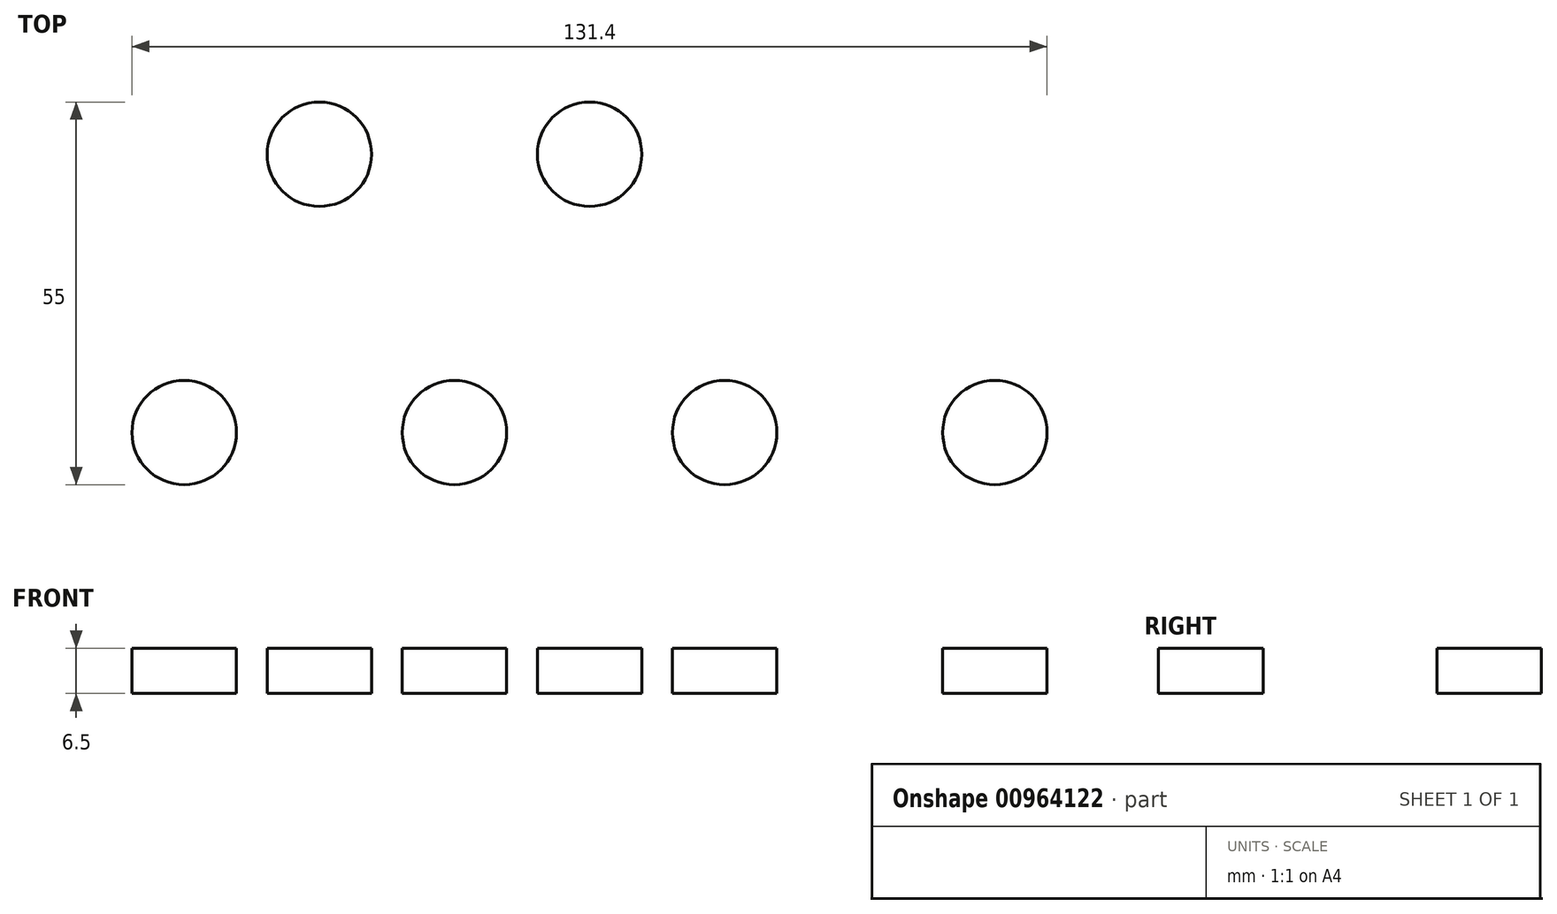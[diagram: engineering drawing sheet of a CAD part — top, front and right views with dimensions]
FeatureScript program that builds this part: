
annotation { "Feature Type Name" : "Feature", "Feature Type Description" : "" }
export const myFeature = defineFeature(function(context is Context, id is Id, definition is map)
    precondition{}
    {
        {
            var Q0;
            Q0=qCreatedBy(makeId("Top.planeOp"),FACE);
            var sketch = newSketch(context, id + "F0", { "sketchPlane" : qUnion([Q0])});
            skLineSegment(sketch, "E0.bottom", {"start": v(-80, 55) * mm, "end": v(80, 55) * mm});
            skLineSegment(sketch, "E0.top", {"start": v(-80, -55) * mm, "end": v(80, -55) * mm});
            skLineSegment(sketch, "E0.left", {"start": v(-80, 55) * mm, "end": v(-80, -55) * mm});
            skLineSegment(sketch, "E0.right", {"start": v(80, 55) * mm, "end": v(80, -55) * mm});
            skPoint(sketch, "E0.middle", {"position": v(0, 0) * mm});
            skSolve(sketch);
        }
        {
            var Q0;
            Q0=makeQuery(id+"F0.imprint","IMPRINT",FACE,{"disambiguationData":[TD([[makeQuery(id+"F0.imprint","IMPRINT",EDGE,{"derivedFrom":sQuery(id+"F0.wireOp",EDGE,"E0.bottom")}),-1.0]])]});
            extrude(context, id + "F1", {"entities" : qUnion([Q0]), "depth" : 6.5 * mm, "offsetDistance" : 25 * mm});
        }
        {
            var Q0;
            Q0=makeQuery(id+"F1.opExtrude","SWEPT_FACE",FACE,{"disambiguationData":[OSD([sQuery(id+"F0.wireOp",EDGE,"E0.left")])]});
            var sketch = newSketch(context, id + "F2", { "sketchPlane" : qUnion([Q0])});
            skLineSegment(sketch, "E1", {"start": v(-55, 3.25) * mm, "end": v(-35, 3.25) * mm});
            skLineSegment(sketch, "E2", {"start": v(-35, 3.25) * mm, "end": v(0, 3.25) * mm});
            skLineSegment(sketch, "E3", {"start": v(0, 3.25) * mm, "end": v(35, 3.25) * mm});
            skLineSegment(sketch, "E4", {"start": v(35, 3.25) * mm, "end": v(55, 3.25) * mm});
            skLineSegment(sketch, "E5.bottom", {"start": v(-39.75, 6.5) * mm, "end": v(-30.25, 6.5) * mm});
            skLineSegment(sketch, "E5.top", {"start": v(-39.75, 0) * mm, "end": v(-30.25, 0) * mm});
            skLineSegment(sketch, "E5.left", {"start": v(-39.75, 6.5) * mm, "end": v(-39.75, 0) * mm});
            skLineSegment(sketch, "E5.right", {"start": v(-30.25, 6.5) * mm, "end": v(-30.25, 0) * mm});
            skPoint(sketch, "E5.middle", {"position": v(-35, 3.25) * mm});
            skLineSegment(sketch, "E6.bottom", {"start": v(-4.75, 6.5) * mm, "end": v(4.75, 6.5) * mm});
            skLineSegment(sketch, "E6.top", {"start": v(-4.75, 0) * mm, "end": v(4.75, 0) * mm});
            skLineSegment(sketch, "E6.left", {"start": v(-4.75, 6.5) * mm, "end": v(-4.75, 0) * mm});
            skLineSegment(sketch, "E6.right", {"start": v(4.75, 6.5) * mm, "end": v(4.75, 0) * mm});
            skPoint(sketch, "E6.middle", {"position": v(0, 3.25) * mm});
            skLineSegment(sketch, "E7.bottom", {"start": v(39.75, 6.5) * mm, "end": v(30.25, 6.5) * mm});
            skLineSegment(sketch, "E7.top", {"start": v(39.75, 0) * mm, "end": v(30.25, 0) * mm});
            skLineSegment(sketch, "E7.left", {"start": v(39.75, 6.5) * mm, "end": v(39.75, 0) * mm});
            skLineSegment(sketch, "E7.right", {"start": v(30.25, 6.5) * mm, "end": v(30.25, 0) * mm});
            skPoint(sketch, "E7.middle", {"position": v(35, 3.25) * mm});
            skSolve(sketch);
        }
        {
            var Q0;
            {var subQ0=sQuery(id+"F2.wireOp",EDGE,"E5.bottom");Q0=makeQuery(id+"F2.imprint","IMPRINT",FACE,{"disambiguationData":[TD([[makeQuery(id+"F2.imprint","IMPRINT",EDGE,{"derivedFrom":subQ0}),-1.0]])]});}
            var Q1;
            {var subQ1=sQuery(id+"F2.wireOp",EDGE,"E5.top");Q1=makeQuery(id+"F2.imprint","IMPRINT",FACE,{"disambiguationData":[TD([[makeQuery(id+"F2.imprint","IMPRINT",EDGE,{"derivedFrom":subQ1}),1.0]])]});}
            var Q2;
            {var subQ1=sQuery(id+"F2.wireOp",EDGE,"E6.bottom");Q2=makeQuery(id+"F2.imprint","IMPRINT",FACE,{"disambiguationData":[TD([[makeQuery(id+"F2.imprint","IMPRINT",EDGE,{"derivedFrom":subQ1}),-1.0]])]});}
            var Q3;
            {var subQ0=sQuery(id+"F2.wireOp",EDGE,"E6.top");Q3=makeQuery(id+"F2.imprint","IMPRINT",FACE,{"disambiguationData":[TD([[makeQuery(id+"F2.imprint","IMPRINT",EDGE,{"derivedFrom":subQ0}),1.0]])]});}
            var Q4;
            {var subQ1=sQuery(id+"F2.wireOp",EDGE,"E7.bottom");Q4=makeQuery(id+"F2.imprint","IMPRINT",FACE,{"disambiguationData":[TD([[makeQuery(id+"F2.imprint","IMPRINT",EDGE,{"derivedFrom":subQ1}),-1.0]])]});}
            var Q5;
            {var subQ1=sQuery(id+"F2.wireOp",EDGE,"E7.top");Q5=makeQuery(id+"F2.imprint","IMPRINT",FACE,{"disambiguationData":[TD([[makeQuery(id+"F2.imprint","IMPRINT",EDGE,{"derivedFrom":subQ1}),1.0]])]});}
            extrude(context, id + "F3", {"entities" : qUnion([Q0, Q1, Q2, Q3, Q4, Q5]), "operationType" : NewBodyOperationType.ADD, "depth" : 6 * mm, "offsetDistance" : 25 * mm});
        }
        {
            var Q0;
            Q0=makeQuery(id+"F1.opExtrude","SWEPT_FACE",FACE,{"disambiguationData":[OSD([sQuery(id+"F0.wireOp",EDGE,"E0.right")])]});
            var sketch = newSketch(context, id + "F4", { "sketchPlane" : qUnion([Q0])});
            skLineSegment(sketch, "E8", {"start": v(-55, 3.25) * mm, "end": v(-35, 3.25) * mm});
            skLineSegment(sketch, "E9", {"start": v(-35, 3.25) * mm, "end": v(0, 3.25) * mm});
            skLineSegment(sketch, "E10", {"start": v(0, 3.25) * mm, "end": v(35, 3.25) * mm});
            skLineSegment(sketch, "E11.bottom", {"start": v(-39.75, 6.5) * mm, "end": v(-30.25, 6.5) * mm});
            skLineSegment(sketch, "E11.top", {"start": v(-39.75, 0) * mm, "end": v(-30.25, 0) * mm});
            skLineSegment(sketch, "E11.left", {"start": v(-39.75, 6.5) * mm, "end": v(-39.75, 0) * mm});
            skLineSegment(sketch, "E11.right", {"start": v(-30.25, 6.5) * mm, "end": v(-30.25, 0) * mm});
            skPoint(sketch, "E11.middle", {"position": v(-35, 3.25) * mm});
            skLineSegment(sketch, "E12.bottom", {"start": v(-4.75, 6.5) * mm, "end": v(4.75, 6.5) * mm});
            skLineSegment(sketch, "E12.top", {"start": v(-4.75, 0) * mm, "end": v(4.75, 0) * mm});
            skLineSegment(sketch, "E12.left", {"start": v(-4.75, 6.5) * mm, "end": v(-4.75, 0) * mm});
            skLineSegment(sketch, "E12.right", {"start": v(4.75, 6.5) * mm, "end": v(4.75, 0) * mm});
            skPoint(sketch, "E12.middle", {"position": v(0, 3.25) * mm});
            skLineSegment(sketch, "E13.bottom", {"start": v(39.75, 6.5) * mm, "end": v(30.25, 6.5) * mm});
            skLineSegment(sketch, "E13.top", {"start": v(39.75, 0) * mm, "end": v(30.25, 0) * mm});
            skLineSegment(sketch, "E13.left", {"start": v(39.75, 6.5) * mm, "end": v(39.75, 0) * mm});
            skLineSegment(sketch, "E13.right", {"start": v(30.25, 6.5) * mm, "end": v(30.25, 0) * mm});
            skPoint(sketch, "E13.middle", {"position": v(35, 3.25) * mm});
            skSolve(sketch);
        }
        {
            var Q0;
            {var subQ1=sQuery(id+"F4.wireOp",EDGE,"E11.bottom");Q0=makeQuery(id+"F4.imprint","IMPRINT",FACE,{"disambiguationData":[TD([[makeQuery(id+"F4.imprint","IMPRINT",EDGE,{"derivedFrom":subQ1}),1.0]])]});}
            var Q1;
            {var subQ1=sQuery(id+"F4.wireOp",EDGE,"E11.top");Q1=makeQuery(id+"F4.imprint","IMPRINT",FACE,{"disambiguationData":[TD([[makeQuery(id+"F4.imprint","IMPRINT",EDGE,{"derivedFrom":subQ1}),-1.0]])]});}
            var Q2;
            {var subQ0=sQuery(id+"F4.wireOp",EDGE,"E12.bottom");Q2=makeQuery(id+"F4.imprint","IMPRINT",FACE,{"disambiguationData":[TD([[makeQuery(id+"F4.imprint","IMPRINT",EDGE,{"derivedFrom":subQ0}),1.0]])]});}
            var Q3;
            {var subQ1=sQuery(id+"F4.wireOp",EDGE,"E12.top");Q3=makeQuery(id+"F4.imprint","IMPRINT",FACE,{"disambiguationData":[TD([[makeQuery(id+"F4.imprint","IMPRINT",EDGE,{"derivedFrom":subQ1}),-1.0]])]});}
            var Q4;
            {var subQ1=sQuery(id+"F4.wireOp",EDGE,"E13.bottom");Q4=makeQuery(id+"F4.imprint","IMPRINT",FACE,{"disambiguationData":[TD([[makeQuery(id+"F4.imprint","IMPRINT",EDGE,{"derivedFrom":subQ1}),1.0]])]});}
            extrude(context, id + "F5", {"entities" : qUnion([Q0, Q1, Q2, Q3, Q4]), "operationType" : NewBodyOperationType.ADD, "depth" : 6 * mm, "offsetDistance" : 25 * mm});
        }
        {
            var Q0;
            Q0=makeQuery(id+"F5.boolean.opBoolean","MERGE",FACE,{"derivedFrom":[makeQuery(id+"F3.boolean.opBoolean","MERGE",FACE,{"derivedFrom":[makeQuery(id+"F1.opExtrude","CAP_FACE",FACE,{"disambiguationData":[OSD([sQuery(id+"F0.wireOp",EDGE,"E0.bottom"),sQuery(id+"F0.wireOp",EDGE,"E0.top"),sQuery(id+"F0.wireOp",EDGE,"E0.left"),sQuery(id+"F0.wireOp",EDGE,"E0.right")])],"isStart":false}),makeQuery(id+"F3.opExtrude","SWEPT_FACE",FACE,{"disambiguationData":[OSD([sQuery(id+"F2.wireOp",EDGE,"E5.bottom")])]}),makeQuery(id+"F3.opExtrude","SWEPT_FACE",FACE,{"disambiguationData":[OSD([sQuery(id+"F2.wireOp",EDGE,"E6.bottom")])]}),makeQuery(id+"F3.opExtrude","SWEPT_FACE",FACE,{"disambiguationData":[OSD([sQuery(id+"F2.wireOp",EDGE,"E7.bottom")])]})]}),makeQuery(id+"F5.opExtrude","SWEPT_FACE",FACE,{"disambiguationData":[OSD([sQuery(id+"F4.wireOp",EDGE,"E11.bottom")])]}),makeQuery(id+"F5.opExtrude","SWEPT_FACE",FACE,{"disambiguationData":[OSD([sQuery(id+"F4.wireOp",EDGE,"E12.bottom")])]}),makeQuery(id+"F5.opExtrude","SWEPT_FACE",FACE,{"disambiguationData":[OSD([sQuery(id+"F4.wireOp",EDGE,"E13.bottom")])]})]});
            var sketch = newSketch(context, id + "F6", { "sketchPlane" : qUnion([Q0])});
            skLineSegment(sketch, "E14", {"start": v(-67.9, 55) * mm, "end": v(-67.9, 40) * mm});
            skLineSegment(sketch, "E15", {"start": v(-67.9, 40) * mm, "end": v(-67.9, 20) * mm});
            skLineSegment(sketch, "E16", {"start": v(-67.9, 20) * mm, "end": v(-67.9, 0) * mm});
            skLineSegment(sketch, "E17", {"start": v(-67.9, 0) * mm, "end": v(-67.9, -20) * mm});
            skLineSegment(sketch, "E18", {"start": v(-67.9, -20) * mm, "end": v(-67.9, -40) * mm});
            skCircle(sketch, "E19", {"center": v(-67.9, 40) * mm, "radius": 7.5 * mm});
            skCircle(sketch, "E20", {"center": v(-67.9, 20) * mm, "radius": 7.5 * mm});
            skCircle(sketch, "E21", {"center": v(-67.9, 0) * mm, "radius": 7.5 * mm});
            skCircle(sketch, "E22", {"center": v(-67.9, -20) * mm, "radius": 7.5 * mm});
            skCircle(sketch, "E23", {"center": v(-67.9, -40) * mm, "radius": 7.5 * mm});
            skLineSegment(sketch, "E24", {"start": v(-48.5, 55) * mm, "end": v(-48.5, -55) * mm});
            skLineSegment(sketch, "E25", {"start": v(-29.1, 55) * mm, "end": v(-29.1, -55) * mm});
            skLineSegment(sketch, "E26", {"start": v(-9.7, 55) * mm, "end": v(-9.7, -55) * mm});
            skLineSegment(sketch, "E27", {"start": v(9.7, -55) * mm, "end": v(9.7, 55) * mm});
            skLineSegment(sketch, "E28", {"start": v(29.1, 55) * mm, "end": v(29.1, -55) * mm});
            skLineSegment(sketch, "E29", {"start": v(48.5, -55) * mm, "end": v(48.5, 55) * mm});
            skLineSegment(sketch, "E30", {"start": v(67.9, 55) * mm, "end": v(67.9, -55) * mm});
            skCircle(sketch, "E31", {"center": v(-48.5, 40) * mm, "radius": 7.99 * mm});
            skCircle(sketch, "E32", {"center": v(-48.5, 20) * mm, "radius": 7.5 * mm});
            skCircle(sketch, "E33", {"center": v(-48.5, 0) * mm, "radius": 7.5 * mm});
            skCircle(sketch, "E34", {"center": v(-48.5, -20) * mm, "radius": 7.5 * mm});
            skCircle(sketch, "E35", {"center": v(-48.5, -40) * mm, "radius": 7.5 * mm});
            skCircle(sketch, "E36.MirrorC", {"center": v(-29.1, 40) * mm, "radius": 7.5 * mm});
            skCircle(sketch, "E37.MirrorC", {"center": v(-29.1, 20) * mm, "radius": 7.5 * mm});
            skCircle(sketch, "E38.MirrorC", {"center": v(-29.1, 0) * mm, "radius": 7.5 * mm});
            skCircle(sketch, "E39.MirrorC", {"center": v(-29.1, -20) * mm, "radius": 7.5 * mm});
            skCircle(sketch, "E40.MirrorC", {"center": v(-29.1, -40) * mm, "radius": 7.5 * mm});
            skCircle(sketch, "E41.MirrorC", {"center": v(-9.7, 40) * mm, "radius": 7.99 * mm});
            skCircle(sketch, "E42.MirrorC", {"center": v(-9.7, 20) * mm, "radius": 7.5 * mm});
            skCircle(sketch, "E43.MirrorC", {"center": v(-9.7, 0) * mm, "radius": 7.5 * mm});
            skCircle(sketch, "E44.MirrorC", {"center": v(-9.7, -20) * mm, "radius": 7.5 * mm});
            skCircle(sketch, "E45.MirrorC", {"center": v(-9.7, -40) * mm, "radius": 7.5 * mm});
            skCircle(sketch, "E46.MirrorC", {"center": v(9.7, 40) * mm, "radius": 7.5 * mm});
            skCircle(sketch, "E47.MirrorC", {"center": v(9.7, 20) * mm, "radius": 7.5 * mm});
            skCircle(sketch, "E48.MirrorC", {"center": v(9.7, 0) * mm, "radius": 7.5 * mm});
            skCircle(sketch, "E49.MirrorC", {"center": v(9.7, -40) * mm, "radius": 7.5 * mm});
            skCircle(sketch, "E50.MirrorC", {"center": v(9.7, -20) * mm, "radius": 7.5 * mm});
            skCircle(sketch, "E51.MirrorC", {"center": v(48.5, 40) * mm, "radius": 7.5 * mm});
            skCircle(sketch, "E52.MirrorC", {"center": v(48.5, 20) * mm, "radius": 7.5 * mm});
            skCircle(sketch, "E53.MirrorC", {"center": v(48.5, 0) * mm, "radius": 7.5 * mm});
            skCircle(sketch, "E54.MirrorC", {"center": v(48.5, -20) * mm, "radius": 7.5 * mm});
            skCircle(sketch, "E55.MirrorC", {"center": v(48.5, -40) * mm, "radius": 7.5 * mm});
            skCircle(sketch, "E56.MirrorC", {"center": v(29.1, 20) * mm, "radius": 7.5 * mm});
            skCircle(sketch, "E57.MirrorC", {"center": v(29.1, 0) * mm, "radius": 7.5 * mm});
            skCircle(sketch, "E58.MirrorC", {"center": v(29.1, 40) * mm, "radius": 7.99 * mm});
            skCircle(sketch, "E59.MirrorC", {"center": v(29.1, -20) * mm, "radius": 7.5 * mm});
            skCircle(sketch, "E60.MirrorC", {"center": v(29.1, -40) * mm, "radius": 7.5 * mm});
            skCircle(sketch, "E61.MirrorC", {"center": v(67.9, 40) * mm, "radius": 7.99 * mm});
            skCircle(sketch, "E62.MirrorC", {"center": v(67.9, 20) * mm, "radius": 7.5 * mm});
            skCircle(sketch, "E63.MirrorC", {"center": v(67.9, 0) * mm, "radius": 7.5 * mm});
            skCircle(sketch, "E64.MirrorC", {"center": v(67.9, -20) * mm, "radius": 7.5 * mm});
            skCircle(sketch, "E65.MirrorC", {"center": v(67.9, -40) * mm, "radius": 7.5 * mm});
            skSolve(sketch);
        }
        {
            var Q0;
            {var subQ0=sQuery(id+"F6.wireOp",EDGE,"E15");var subQ1=sQuery(id+"F6.wireOp",EDGE,"E14");var subQ2=makeQuery(id+"F6.imprint","INTERSECT",VERTEX,{"derivedFrom":[subQ1,subQ0]});Q0=makeQuery(id+"F6.imprint","IMPRINT",FACE,{"disambiguationData":[TD([[makeQuery(id+"F6.imprint","IMPRINT",EDGE,{"disambiguationData":[TD([[subQ2,1.0]])],"derivedFrom":subQ1}),-1.0]])]});}
            var Q1;
            {var subQ0=sQuery(id+"F6.wireOp",EDGE,"E15");var subQ1=sQuery(id+"F6.wireOp",EDGE,"E14");var subQ2=makeQuery(id+"F6.imprint","INTERSECT",VERTEX,{"derivedFrom":[subQ1,subQ0]});Q1=makeQuery(id+"F6.imprint","IMPRINT",FACE,{"disambiguationData":[TD([[makeQuery(id+"F6.imprint","IMPRINT",EDGE,{"disambiguationData":[TD([[subQ2,1.0]])],"derivedFrom":subQ1}),1.0]])]});}
            var Q2;
            {var subQ0=sQuery(id+"F6.wireOp",EDGE,"E31");var subQ1=sQuery(id+"F6.wireOp",EDGE,"E24");var subQ2=makeQuery(id+"F6.imprint","INTERSECT",VERTEX,{"disambiguationData":[OD(0.0)],"derivedFrom":[subQ1,subQ0]});Q2=makeQuery(id+"F6.imprint","IMPRINT",FACE,{"disambiguationData":[TD([[makeQuery(id+"F6.imprint","IMPRINT",EDGE,{"disambiguationData":[TD([[subQ2,-1.0]])],"derivedFrom":subQ1}),-1.0]])]});}
            var Q3;
            {var subQ0=sQuery(id+"F6.wireOp",EDGE,"E31");var subQ1=sQuery(id+"F6.wireOp",EDGE,"E24");var subQ2=makeQuery(id+"F6.imprint","INTERSECT",VERTEX,{"disambiguationData":[OD(0.0)],"derivedFrom":[subQ1,subQ0]});Q3=makeQuery(id+"F6.imprint","IMPRINT",FACE,{"disambiguationData":[TD([[makeQuery(id+"F6.imprint","IMPRINT",EDGE,{"disambiguationData":[TD([[subQ2,-1.0]])],"derivedFrom":subQ1}),1.0]])]});}
            var Q4;
            {var subQ0=sQuery(id+"F6.wireOp",EDGE,"E36.MirrorC");var subQ1=sQuery(id+"F6.wireOp",EDGE,"E25");var subQ2=makeQuery(id+"F6.imprint","INTERSECT",VERTEX,{"disambiguationData":[OD(0.0)],"derivedFrom":[subQ1,subQ0]});Q4=makeQuery(id+"F6.imprint","IMPRINT",FACE,{"disambiguationData":[TD([[makeQuery(id+"F6.imprint","IMPRINT",EDGE,{"disambiguationData":[TD([[subQ2,-1.0]])],"derivedFrom":subQ1}),-1.0]])]});}
            var Q5;
            {var subQ0=sQuery(id+"F6.wireOp",EDGE,"E36.MirrorC");var subQ1=sQuery(id+"F6.wireOp",EDGE,"E25");var subQ2=makeQuery(id+"F6.imprint","INTERSECT",VERTEX,{"disambiguationData":[OD(0.0)],"derivedFrom":[subQ1,subQ0]});Q5=makeQuery(id+"F6.imprint","IMPRINT",FACE,{"disambiguationData":[TD([[makeQuery(id+"F6.imprint","IMPRINT",EDGE,{"disambiguationData":[TD([[subQ2,-1.0]])],"derivedFrom":subQ1}),1.0]])]});}
            var Q6;
            {var subQ0=sQuery(id+"F6.wireOp",EDGE,"E41.MirrorC");var subQ1=sQuery(id+"F6.wireOp",EDGE,"E26");var subQ2=makeQuery(id+"F6.imprint","INTERSECT",VERTEX,{"disambiguationData":[OD(0.0)],"derivedFrom":[subQ1,subQ0]});Q6=makeQuery(id+"F6.imprint","IMPRINT",FACE,{"disambiguationData":[TD([[makeQuery(id+"F6.imprint","IMPRINT",EDGE,{"disambiguationData":[TD([[subQ2,-1.0]])],"derivedFrom":subQ1}),-1.0]])]});}
            var Q7;
            {var subQ0=sQuery(id+"F6.wireOp",EDGE,"E41.MirrorC");var subQ1=sQuery(id+"F6.wireOp",EDGE,"E26");var subQ2=makeQuery(id+"F6.imprint","INTERSECT",VERTEX,{"disambiguationData":[OD(0.0)],"derivedFrom":[subQ1,subQ0]});Q7=makeQuery(id+"F6.imprint","IMPRINT",FACE,{"disambiguationData":[TD([[makeQuery(id+"F6.imprint","IMPRINT",EDGE,{"disambiguationData":[TD([[subQ2,-1.0]])],"derivedFrom":subQ1}),1.0]])]});}
            var Q8;
            {var subQ0=sQuery(id+"F6.wireOp",EDGE,"E46.MirrorC");var subQ1=sQuery(id+"F6.wireOp",EDGE,"E27");var subQ2=makeQuery(id+"F6.imprint","INTERSECT",VERTEX,{"disambiguationData":[OD(0.0)],"derivedFrom":[subQ1,subQ0]});Q8=makeQuery(id+"F6.imprint","IMPRINT",FACE,{"disambiguationData":[TD([[makeQuery(id+"F6.imprint","IMPRINT",EDGE,{"disambiguationData":[TD([[subQ2,-1.0]])],"derivedFrom":subQ1}),1.0]])]});}
            var Q9;
            {var subQ0=sQuery(id+"F6.wireOp",EDGE,"E46.MirrorC");var subQ1=sQuery(id+"F6.wireOp",EDGE,"E27");var subQ2=makeQuery(id+"F6.imprint","INTERSECT",VERTEX,{"disambiguationData":[OD(0.0)],"derivedFrom":[subQ1,subQ0]});Q9=makeQuery(id+"F6.imprint","IMPRINT",FACE,{"disambiguationData":[TD([[makeQuery(id+"F6.imprint","IMPRINT",EDGE,{"disambiguationData":[TD([[subQ2,-1.0]])],"derivedFrom":subQ1}),-1.0]])]});}
            var Q10;
            {var subQ0=sQuery(id+"F6.wireOp",EDGE,"E58.MirrorC");var subQ1=sQuery(id+"F6.wireOp",EDGE,"E28");var subQ2=makeQuery(id+"F6.imprint","INTERSECT",VERTEX,{"disambiguationData":[OD(0.0)],"derivedFrom":[subQ1,subQ0]});Q10=makeQuery(id+"F6.imprint","IMPRINT",FACE,{"disambiguationData":[TD([[makeQuery(id+"F6.imprint","IMPRINT",EDGE,{"disambiguationData":[TD([[subQ2,-1.0]])],"derivedFrom":subQ1}),-1.0]])]});}
            var Q11;
            {var subQ0=sQuery(id+"F6.wireOp",EDGE,"E58.MirrorC");var subQ1=sQuery(id+"F6.wireOp",EDGE,"E28");var subQ2=makeQuery(id+"F6.imprint","INTERSECT",VERTEX,{"disambiguationData":[OD(0.0)],"derivedFrom":[subQ1,subQ0]});Q11=makeQuery(id+"F6.imprint","IMPRINT",FACE,{"disambiguationData":[TD([[makeQuery(id+"F6.imprint","IMPRINT",EDGE,{"disambiguationData":[TD([[subQ2,-1.0]])],"derivedFrom":subQ1}),1.0]])]});}
            var Q12;
            {var subQ0=sQuery(id+"F6.wireOp",EDGE,"E51.MirrorC");var subQ1=sQuery(id+"F6.wireOp",EDGE,"E29");var subQ2=makeQuery(id+"F6.imprint","INTERSECT",VERTEX,{"disambiguationData":[OD(0.0)],"derivedFrom":[subQ1,subQ0]});Q12=makeQuery(id+"F6.imprint","IMPRINT",FACE,{"disambiguationData":[TD([[makeQuery(id+"F6.imprint","IMPRINT",EDGE,{"disambiguationData":[TD([[subQ2,-1.0]])],"derivedFrom":subQ1}),1.0]])]});}
            var Q13;
            {var subQ0=sQuery(id+"F6.wireOp",EDGE,"E51.MirrorC");var subQ1=sQuery(id+"F6.wireOp",EDGE,"E29");var subQ2=makeQuery(id+"F6.imprint","INTERSECT",VERTEX,{"disambiguationData":[OD(0.0)],"derivedFrom":[subQ1,subQ0]});Q13=makeQuery(id+"F6.imprint","IMPRINT",FACE,{"disambiguationData":[TD([[makeQuery(id+"F6.imprint","IMPRINT",EDGE,{"disambiguationData":[TD([[subQ2,-1.0]])],"derivedFrom":subQ1}),-1.0]])]});}
            var Q14;
            {var subQ0=sQuery(id+"F6.wireOp",EDGE,"E61.MirrorC");var subQ1=sQuery(id+"F6.wireOp",EDGE,"E30");var subQ2=makeQuery(id+"F6.imprint","INTERSECT",VERTEX,{"disambiguationData":[OD(0.0)],"derivedFrom":[subQ1,subQ0]});Q14=makeQuery(id+"F6.imprint","IMPRINT",FACE,{"disambiguationData":[TD([[makeQuery(id+"F6.imprint","IMPRINT",EDGE,{"disambiguationData":[TD([[subQ2,-1.0]])],"derivedFrom":subQ1}),-1.0]])]});}
            var Q15;
            {var subQ0=sQuery(id+"F6.wireOp",EDGE,"E61.MirrorC");var subQ1=sQuery(id+"F6.wireOp",EDGE,"E30");var subQ2=makeQuery(id+"F6.imprint","INTERSECT",VERTEX,{"disambiguationData":[OD(0.0)],"derivedFrom":[subQ1,subQ0]});Q15=makeQuery(id+"F6.imprint","IMPRINT",FACE,{"disambiguationData":[TD([[makeQuery(id+"F6.imprint","IMPRINT",EDGE,{"disambiguationData":[TD([[subQ2,-1.0]])],"derivedFrom":subQ1}),1.0]])]});}
            var Q16;
            {var subQ0=sQuery(id+"F6.wireOp",EDGE,"f1a9cb92-975a-438b-a2d5-9edff02349330.MirrorC");var subQ1=sQuery(id+"F6.wireOp",EDGE,"O4PxhCDK-rAjw-q9Xn-edEA-3iuNw1oMgCf9");var subQ2=makeQuery(id+"F6.imprint","INTERSECT",VERTEX,{"disambiguationData":[OD(0.0)],"derivedFrom":[subQ1,subQ0]});Q16=makeQuery(id+"F6.imprint","IMPRINT",FACE,{"disambiguationData":[TD([[makeQuery(id+"F6.imprint","IMPRINT",EDGE,{"disambiguationData":[TD([[subQ2,-1.0]])],"derivedFrom":subQ1}),-1.0]])]});}
            var Q17;
            {var subQ0=sQuery(id+"F6.wireOp",EDGE,"f1a9cb92-975a-438b-a2d5-9edff02349330.MirrorC");var subQ1=sQuery(id+"F6.wireOp",EDGE,"O4PxhCDK-rAjw-q9Xn-edEA-3iuNw1oMgCf9");var subQ2=makeQuery(id+"F6.imprint","INTERSECT",VERTEX,{"disambiguationData":[OD(0.0)],"derivedFrom":[subQ1,subQ0]});Q17=makeQuery(id+"F6.imprint","IMPRINT",FACE,{"disambiguationData":[TD([[makeQuery(id+"F6.imprint","IMPRINT",EDGE,{"disambiguationData":[TD([[subQ2,-1.0]])],"derivedFrom":subQ1}),1.0]])]});}
            var Q18;
            {var subQ0=sQuery(id+"F6.wireOp",EDGE,"1bc8c645-9b15-42f9-900e-afe118bcb0160.MirrorC");var subQ1=sQuery(id+"F6.wireOp",EDGE,"eJEehShp-Jti8-Zoit-Wwds-1zDcvAIGxxXx");var subQ2=makeQuery(id+"F6.imprint","INTERSECT",VERTEX,{"disambiguationData":[OD(0.0)],"derivedFrom":[subQ1,subQ0]});Q18=makeQuery(id+"F6.imprint","IMPRINT",FACE,{"disambiguationData":[TD([[makeQuery(id+"F6.imprint","IMPRINT",EDGE,{"disambiguationData":[TD([[subQ2,-1.0]])],"derivedFrom":subQ1}),-1.0]])]});}
            var Q19;
            {var subQ0=sQuery(id+"F6.wireOp",EDGE,"1bc8c645-9b15-42f9-900e-afe118bcb0160.MirrorC");var subQ1=sQuery(id+"F6.wireOp",EDGE,"eJEehShp-Jti8-Zoit-Wwds-1zDcvAIGxxXx");var subQ2=makeQuery(id+"F6.imprint","INTERSECT",VERTEX,{"disambiguationData":[OD(0.0)],"derivedFrom":[subQ1,subQ0]});Q19=makeQuery(id+"F6.imprint","IMPRINT",FACE,{"disambiguationData":[TD([[makeQuery(id+"F6.imprint","IMPRINT",EDGE,{"disambiguationData":[TD([[subQ2,-1.0]])],"derivedFrom":subQ1}),1.0]])]});}
            var Q20;
            {var subQ0=sQuery(id+"F6.wireOp",EDGE,"ba6fe1b2-4239-4431-82f9-d2fa67060a230.MirrorC");var subQ1=sQuery(id+"F6.wireOp",EDGE,"eJEehShp-Jti8-Zoit-Wwds-1zDcvAIGxxXx");var subQ2=makeQuery(id+"F6.imprint","INTERSECT",VERTEX,{"disambiguationData":[OD(0.0)],"derivedFrom":[subQ1,subQ0]});Q20=makeQuery(id+"F6.imprint","IMPRINT",FACE,{"disambiguationData":[TD([[makeQuery(id+"F6.imprint","IMPRINT",EDGE,{"disambiguationData":[TD([[subQ2,-1.0]])],"derivedFrom":subQ1}),1.0]])]});}
            var Q21;
            {var subQ0=sQuery(id+"F6.wireOp",EDGE,"ba6fe1b2-4239-4431-82f9-d2fa67060a230.MirrorC");var subQ1=sQuery(id+"F6.wireOp",EDGE,"eJEehShp-Jti8-Zoit-Wwds-1zDcvAIGxxXx");var subQ2=makeQuery(id+"F6.imprint","INTERSECT",VERTEX,{"disambiguationData":[OD(0.0)],"derivedFrom":[subQ1,subQ0]});Q21=makeQuery(id+"F6.imprint","IMPRINT",FACE,{"disambiguationData":[TD([[makeQuery(id+"F6.imprint","IMPRINT",EDGE,{"disambiguationData":[TD([[subQ2,-1.0]])],"derivedFrom":subQ1}),-1.0]])]});}
            var Q22;
            {var subQ0=sQuery(id+"F6.wireOp",EDGE,"204b8fe5-7456-48cf-b7e5-ad05656423dc0.MirrorC");var subQ1=sQuery(id+"F6.wireOp",EDGE,"O4PxhCDK-rAjw-q9Xn-edEA-3iuNw1oMgCf9");var subQ2=makeQuery(id+"F6.imprint","INTERSECT",VERTEX,{"disambiguationData":[OD(0.0)],"derivedFrom":[subQ1,subQ0]});Q22=makeQuery(id+"F6.imprint","IMPRINT",FACE,{"disambiguationData":[TD([[makeQuery(id+"F6.imprint","IMPRINT",EDGE,{"disambiguationData":[TD([[subQ2,-1.0]])],"derivedFrom":subQ1}),1.0]])]});}
            var Q23;
            {var subQ0=sQuery(id+"F6.wireOp",EDGE,"204b8fe5-7456-48cf-b7e5-ad05656423dc0.MirrorC");var subQ1=sQuery(id+"F6.wireOp",EDGE,"O4PxhCDK-rAjw-q9Xn-edEA-3iuNw1oMgCf9");var subQ2=makeQuery(id+"F6.imprint","INTERSECT",VERTEX,{"disambiguationData":[OD(0.0)],"derivedFrom":[subQ1,subQ0]});Q23=makeQuery(id+"F6.imprint","IMPRINT",FACE,{"disambiguationData":[TD([[makeQuery(id+"F6.imprint","IMPRINT",EDGE,{"disambiguationData":[TD([[subQ2,-1.0]])],"derivedFrom":subQ1}),-1.0]])]});}
            var Q24;
            {var subQ0=sQuery(id+"F6.wireOp",EDGE,"E62.MirrorC");var subQ1=sQuery(id+"F6.wireOp",EDGE,"E30");var subQ2=makeQuery(id+"F6.imprint","INTERSECT",VERTEX,{"disambiguationData":[OD(0.0)],"derivedFrom":[subQ1,subQ0]});Q24=makeQuery(id+"F6.imprint","IMPRINT",FACE,{"disambiguationData":[TD([[makeQuery(id+"F6.imprint","IMPRINT",EDGE,{"disambiguationData":[TD([[subQ2,-1.0]])],"derivedFrom":subQ1}),1.0]])]});}
            var Q25;
            {var subQ0=sQuery(id+"F6.wireOp",EDGE,"E62.MirrorC");var subQ1=sQuery(id+"F6.wireOp",EDGE,"E30");var subQ2=makeQuery(id+"F6.imprint","INTERSECT",VERTEX,{"disambiguationData":[OD(0.0)],"derivedFrom":[subQ1,subQ0]});Q25=makeQuery(id+"F6.imprint","IMPRINT",FACE,{"disambiguationData":[TD([[makeQuery(id+"F6.imprint","IMPRINT",EDGE,{"disambiguationData":[TD([[subQ2,-1.0]])],"derivedFrom":subQ1}),-1.0]])]});}
            var Q26;
            {var subQ0=sQuery(id+"F6.wireOp",EDGE,"E52.MirrorC");var subQ1=sQuery(id+"F6.wireOp",EDGE,"E29");var subQ2=makeQuery(id+"F6.imprint","INTERSECT",VERTEX,{"disambiguationData":[OD(0.0)],"derivedFrom":[subQ1,subQ0]});Q26=makeQuery(id+"F6.imprint","IMPRINT",FACE,{"disambiguationData":[TD([[makeQuery(id+"F6.imprint","IMPRINT",EDGE,{"disambiguationData":[TD([[subQ2,-1.0]])],"derivedFrom":subQ1}),-1.0]])]});}
            var Q27;
            {var subQ0=sQuery(id+"F6.wireOp",EDGE,"E52.MirrorC");var subQ1=sQuery(id+"F6.wireOp",EDGE,"E29");var subQ2=makeQuery(id+"F6.imprint","INTERSECT",VERTEX,{"disambiguationData":[OD(0.0)],"derivedFrom":[subQ1,subQ0]});Q27=makeQuery(id+"F6.imprint","IMPRINT",FACE,{"disambiguationData":[TD([[makeQuery(id+"F6.imprint","IMPRINT",EDGE,{"disambiguationData":[TD([[subQ2,-1.0]])],"derivedFrom":subQ1}),1.0]])]});}
            var Q28;
            {var subQ0=sQuery(id+"F6.wireOp",EDGE,"E56.MirrorC");var subQ1=sQuery(id+"F6.wireOp",EDGE,"E28");var subQ2=makeQuery(id+"F6.imprint","INTERSECT",VERTEX,{"disambiguationData":[OD(0.0)],"derivedFrom":[subQ1,subQ0]});Q28=makeQuery(id+"F6.imprint","IMPRINT",FACE,{"disambiguationData":[TD([[makeQuery(id+"F6.imprint","IMPRINT",EDGE,{"disambiguationData":[TD([[subQ2,-1.0]])],"derivedFrom":subQ1}),1.0]])]});}
            var Q29;
            {var subQ0=sQuery(id+"F6.wireOp",EDGE,"E56.MirrorC");var subQ1=sQuery(id+"F6.wireOp",EDGE,"E28");var subQ2=makeQuery(id+"F6.imprint","INTERSECT",VERTEX,{"disambiguationData":[OD(0.0)],"derivedFrom":[subQ1,subQ0]});Q29=makeQuery(id+"F6.imprint","IMPRINT",FACE,{"disambiguationData":[TD([[makeQuery(id+"F6.imprint","IMPRINT",EDGE,{"disambiguationData":[TD([[subQ2,-1.0]])],"derivedFrom":subQ1}),-1.0]])]});}
            var Q30;
            {var subQ0=sQuery(id+"F6.wireOp",EDGE,"E47.MirrorC");var subQ1=sQuery(id+"F6.wireOp",EDGE,"E27");var subQ2=makeQuery(id+"F6.imprint","INTERSECT",VERTEX,{"disambiguationData":[OD(0.0)],"derivedFrom":[subQ1,subQ0]});Q30=makeQuery(id+"F6.imprint","IMPRINT",FACE,{"disambiguationData":[TD([[makeQuery(id+"F6.imprint","IMPRINT",EDGE,{"disambiguationData":[TD([[subQ2,-1.0]])],"derivedFrom":subQ1}),-1.0]])]});}
            var Q31;
            {var subQ0=sQuery(id+"F6.wireOp",EDGE,"E47.MirrorC");var subQ1=sQuery(id+"F6.wireOp",EDGE,"E27");var subQ2=makeQuery(id+"F6.imprint","INTERSECT",VERTEX,{"disambiguationData":[OD(0.0)],"derivedFrom":[subQ1,subQ0]});Q31=makeQuery(id+"F6.imprint","IMPRINT",FACE,{"disambiguationData":[TD([[makeQuery(id+"F6.imprint","IMPRINT",EDGE,{"disambiguationData":[TD([[subQ2,-1.0]])],"derivedFrom":subQ1}),1.0]])]});}
            var Q32;
            {var subQ0=sQuery(id+"F6.wireOp",EDGE,"E42.MirrorC");var subQ1=sQuery(id+"F6.wireOp",EDGE,"E26");var subQ2=makeQuery(id+"F6.imprint","INTERSECT",VERTEX,{"disambiguationData":[OD(0.0)],"derivedFrom":[subQ1,subQ0]});Q32=makeQuery(id+"F6.imprint","IMPRINT",FACE,{"disambiguationData":[TD([[makeQuery(id+"F6.imprint","IMPRINT",EDGE,{"disambiguationData":[TD([[subQ2,-1.0]])],"derivedFrom":subQ1}),1.0]])]});}
            var Q33;
            {var subQ0=sQuery(id+"F6.wireOp",EDGE,"E42.MirrorC");var subQ1=sQuery(id+"F6.wireOp",EDGE,"E26");var subQ2=makeQuery(id+"F6.imprint","INTERSECT",VERTEX,{"disambiguationData":[OD(0.0)],"derivedFrom":[subQ1,subQ0]});Q33=makeQuery(id+"F6.imprint","IMPRINT",FACE,{"disambiguationData":[TD([[makeQuery(id+"F6.imprint","IMPRINT",EDGE,{"disambiguationData":[TD([[subQ2,-1.0]])],"derivedFrom":subQ1}),-1.0]])]});}
            var Q34;
            {var subQ0=sQuery(id+"F6.wireOp",EDGE,"E37.MirrorC");var subQ1=sQuery(id+"F6.wireOp",EDGE,"E25");var subQ2=makeQuery(id+"F6.imprint","INTERSECT",VERTEX,{"disambiguationData":[OD(0.0)],"derivedFrom":[subQ1,subQ0]});Q34=makeQuery(id+"F6.imprint","IMPRINT",FACE,{"disambiguationData":[TD([[makeQuery(id+"F6.imprint","IMPRINT",EDGE,{"disambiguationData":[TD([[subQ2,-1.0]])],"derivedFrom":subQ1}),1.0]])]});}
            var Q35;
            {var subQ0=sQuery(id+"F6.wireOp",EDGE,"E37.MirrorC");var subQ1=sQuery(id+"F6.wireOp",EDGE,"E25");var subQ2=makeQuery(id+"F6.imprint","INTERSECT",VERTEX,{"disambiguationData":[OD(0.0)],"derivedFrom":[subQ1,subQ0]});Q35=makeQuery(id+"F6.imprint","IMPRINT",FACE,{"disambiguationData":[TD([[makeQuery(id+"F6.imprint","IMPRINT",EDGE,{"disambiguationData":[TD([[subQ2,-1.0]])],"derivedFrom":subQ1}),-1.0]])]});}
            var Q36;
            {var subQ0=sQuery(id+"F6.wireOp",EDGE,"E32");var subQ1=sQuery(id+"F6.wireOp",EDGE,"E24");var subQ2=makeQuery(id+"F6.imprint","INTERSECT",VERTEX,{"disambiguationData":[OD(0.0)],"derivedFrom":[subQ1,subQ0]});Q36=makeQuery(id+"F6.imprint","IMPRINT",FACE,{"disambiguationData":[TD([[makeQuery(id+"F6.imprint","IMPRINT",EDGE,{"disambiguationData":[TD([[subQ2,-1.0]])],"derivedFrom":subQ1}),1.0]])]});}
            var Q37;
            {var subQ0=sQuery(id+"F6.wireOp",EDGE,"E32");var subQ1=sQuery(id+"F6.wireOp",EDGE,"E24");var subQ2=makeQuery(id+"F6.imprint","INTERSECT",VERTEX,{"disambiguationData":[OD(0.0)],"derivedFrom":[subQ1,subQ0]});Q37=makeQuery(id+"F6.imprint","IMPRINT",FACE,{"disambiguationData":[TD([[makeQuery(id+"F6.imprint","IMPRINT",EDGE,{"disambiguationData":[TD([[subQ2,-1.0]])],"derivedFrom":subQ1}),-1.0]])]});}
            var Q38;
            {var subQ0=sQuery(id+"F6.wireOp",EDGE,"E16");var subQ1=sQuery(id+"F6.wireOp",EDGE,"E15");var subQ2=makeQuery(id+"F6.imprint","INTERSECT",VERTEX,{"derivedFrom":[subQ1,subQ0]});Q38=makeQuery(id+"F6.imprint","IMPRINT",FACE,{"disambiguationData":[TD([[makeQuery(id+"F6.imprint","IMPRINT",EDGE,{"disambiguationData":[TD([[subQ2,1.0]])],"derivedFrom":subQ1}),1.0]])]});}
            var Q39;
            {var subQ0=sQuery(id+"F6.wireOp",EDGE,"E16");var subQ1=sQuery(id+"F6.wireOp",EDGE,"E15");var subQ2=makeQuery(id+"F6.imprint","INTERSECT",VERTEX,{"derivedFrom":[subQ1,subQ0]});Q39=makeQuery(id+"F6.imprint","IMPRINT",FACE,{"disambiguationData":[TD([[makeQuery(id+"F6.imprint","IMPRINT",EDGE,{"disambiguationData":[TD([[subQ2,1.0]])],"derivedFrom":subQ1}),-1.0]])]});}
            var Q40;
            {var subQ0=sQuery(id+"F6.wireOp",EDGE,"E17");var subQ1=sQuery(id+"F6.wireOp",EDGE,"E16");var subQ2=makeQuery(id+"F6.imprint","INTERSECT",VERTEX,{"derivedFrom":[subQ1,subQ0]});Q40=makeQuery(id+"F6.imprint","IMPRINT",FACE,{"disambiguationData":[TD([[makeQuery(id+"F6.imprint","IMPRINT",EDGE,{"disambiguationData":[TD([[subQ2,1.0]])],"derivedFrom":subQ1}),-1.0]])]});}
            var Q41;
            {var subQ0=sQuery(id+"F6.wireOp",EDGE,"E17");var subQ1=sQuery(id+"F6.wireOp",EDGE,"E16");var subQ2=makeQuery(id+"F6.imprint","INTERSECT",VERTEX,{"derivedFrom":[subQ1,subQ0]});Q41=makeQuery(id+"F6.imprint","IMPRINT",FACE,{"disambiguationData":[TD([[makeQuery(id+"F6.imprint","IMPRINT",EDGE,{"disambiguationData":[TD([[subQ2,1.0]])],"derivedFrom":subQ1}),1.0]])]});}
            var Q42;
            {var subQ0=sQuery(id+"F6.wireOp",EDGE,"E33");var subQ1=sQuery(id+"F6.wireOp",EDGE,"E24");var subQ2=makeQuery(id+"F6.imprint","INTERSECT",VERTEX,{"disambiguationData":[OD(0.0)],"derivedFrom":[subQ1,subQ0]});Q42=makeQuery(id+"F6.imprint","IMPRINT",FACE,{"disambiguationData":[TD([[makeQuery(id+"F6.imprint","IMPRINT",EDGE,{"disambiguationData":[TD([[subQ2,-1.0]])],"derivedFrom":subQ1}),-1.0]])]});}
            var Q43;
            {var subQ0=sQuery(id+"F6.wireOp",EDGE,"E33");var subQ1=sQuery(id+"F6.wireOp",EDGE,"E24");var subQ2=makeQuery(id+"F6.imprint","INTERSECT",VERTEX,{"disambiguationData":[OD(0.0)],"derivedFrom":[subQ1,subQ0]});Q43=makeQuery(id+"F6.imprint","IMPRINT",FACE,{"disambiguationData":[TD([[makeQuery(id+"F6.imprint","IMPRINT",EDGE,{"disambiguationData":[TD([[subQ2,-1.0]])],"derivedFrom":subQ1}),1.0]])]});}
            var Q44;
            {var subQ0=sQuery(id+"F6.wireOp",EDGE,"E38.MirrorC");var subQ1=sQuery(id+"F6.wireOp",EDGE,"E25");var subQ2=makeQuery(id+"F6.imprint","INTERSECT",VERTEX,{"disambiguationData":[OD(0.0)],"derivedFrom":[subQ1,subQ0]});Q44=makeQuery(id+"F6.imprint","IMPRINT",FACE,{"disambiguationData":[TD([[makeQuery(id+"F6.imprint","IMPRINT",EDGE,{"disambiguationData":[TD([[subQ2,-1.0]])],"derivedFrom":subQ1}),-1.0]])]});}
            var Q45;
            {var subQ0=sQuery(id+"F6.wireOp",EDGE,"E38.MirrorC");var subQ1=sQuery(id+"F6.wireOp",EDGE,"E25");var subQ2=makeQuery(id+"F6.imprint","INTERSECT",VERTEX,{"disambiguationData":[OD(0.0)],"derivedFrom":[subQ1,subQ0]});Q45=makeQuery(id+"F6.imprint","IMPRINT",FACE,{"disambiguationData":[TD([[makeQuery(id+"F6.imprint","IMPRINT",EDGE,{"disambiguationData":[TD([[subQ2,-1.0]])],"derivedFrom":subQ1}),1.0]])]});}
            var Q46;
            {var subQ0=sQuery(id+"F6.wireOp",EDGE,"E43.MirrorC");var subQ1=sQuery(id+"F6.wireOp",EDGE,"E26");var subQ2=makeQuery(id+"F6.imprint","INTERSECT",VERTEX,{"disambiguationData":[OD(0.0)],"derivedFrom":[subQ1,subQ0]});Q46=makeQuery(id+"F6.imprint","IMPRINT",FACE,{"disambiguationData":[TD([[makeQuery(id+"F6.imprint","IMPRINT",EDGE,{"disambiguationData":[TD([[subQ2,-1.0]])],"derivedFrom":subQ1}),-1.0]])]});}
            var Q47;
            {var subQ0=sQuery(id+"F6.wireOp",EDGE,"E43.MirrorC");var subQ1=sQuery(id+"F6.wireOp",EDGE,"E26");var subQ2=makeQuery(id+"F6.imprint","INTERSECT",VERTEX,{"disambiguationData":[OD(0.0)],"derivedFrom":[subQ1,subQ0]});Q47=makeQuery(id+"F6.imprint","IMPRINT",FACE,{"disambiguationData":[TD([[makeQuery(id+"F6.imprint","IMPRINT",EDGE,{"disambiguationData":[TD([[subQ2,-1.0]])],"derivedFrom":subQ1}),1.0]])]});}
            var Q48;
            {var subQ0=sQuery(id+"F6.wireOp",EDGE,"E48.MirrorC");var subQ1=sQuery(id+"F6.wireOp",EDGE,"E27");var subQ2=makeQuery(id+"F6.imprint","INTERSECT",VERTEX,{"disambiguationData":[OD(0.0)],"derivedFrom":[subQ1,subQ0]});Q48=makeQuery(id+"F6.imprint","IMPRINT",FACE,{"disambiguationData":[TD([[makeQuery(id+"F6.imprint","IMPRINT",EDGE,{"disambiguationData":[TD([[subQ2,-1.0]])],"derivedFrom":subQ1}),1.0]])]});}
            var Q49;
            {var subQ0=sQuery(id+"F6.wireOp",EDGE,"E48.MirrorC");var subQ1=sQuery(id+"F6.wireOp",EDGE,"E27");var subQ2=makeQuery(id+"F6.imprint","INTERSECT",VERTEX,{"disambiguationData":[OD(0.0)],"derivedFrom":[subQ1,subQ0]});Q49=makeQuery(id+"F6.imprint","IMPRINT",FACE,{"disambiguationData":[TD([[makeQuery(id+"F6.imprint","IMPRINT",EDGE,{"disambiguationData":[TD([[subQ2,-1.0]])],"derivedFrom":subQ1}),-1.0]])]});}
            var Q50;
            {var subQ0=sQuery(id+"F6.wireOp",EDGE,"E57.MirrorC");var subQ1=sQuery(id+"F6.wireOp",EDGE,"E28");var subQ2=makeQuery(id+"F6.imprint","INTERSECT",VERTEX,{"disambiguationData":[OD(0.0)],"derivedFrom":[subQ1,subQ0]});Q50=makeQuery(id+"F6.imprint","IMPRINT",FACE,{"disambiguationData":[TD([[makeQuery(id+"F6.imprint","IMPRINT",EDGE,{"disambiguationData":[TD([[subQ2,-1.0]])],"derivedFrom":subQ1}),-1.0]])]});}
            var Q51;
            {var subQ0=sQuery(id+"F6.wireOp",EDGE,"E57.MirrorC");var subQ1=sQuery(id+"F6.wireOp",EDGE,"E28");var subQ2=makeQuery(id+"F6.imprint","INTERSECT",VERTEX,{"disambiguationData":[OD(0.0)],"derivedFrom":[subQ1,subQ0]});Q51=makeQuery(id+"F6.imprint","IMPRINT",FACE,{"disambiguationData":[TD([[makeQuery(id+"F6.imprint","IMPRINT",EDGE,{"disambiguationData":[TD([[subQ2,-1.0]])],"derivedFrom":subQ1}),1.0]])]});}
            var Q52;
            {var subQ0=sQuery(id+"F6.wireOp",EDGE,"E53.MirrorC");var subQ1=sQuery(id+"F6.wireOp",EDGE,"E29");var subQ2=makeQuery(id+"F6.imprint","INTERSECT",VERTEX,{"disambiguationData":[OD(0.0)],"derivedFrom":[subQ1,subQ0]});Q52=makeQuery(id+"F6.imprint","IMPRINT",FACE,{"disambiguationData":[TD([[makeQuery(id+"F6.imprint","IMPRINT",EDGE,{"disambiguationData":[TD([[subQ2,-1.0]])],"derivedFrom":subQ1}),1.0]])]});}
            var Q53;
            {var subQ0=sQuery(id+"F6.wireOp",EDGE,"E53.MirrorC");var subQ1=sQuery(id+"F6.wireOp",EDGE,"E29");var subQ2=makeQuery(id+"F6.imprint","INTERSECT",VERTEX,{"disambiguationData":[OD(0.0)],"derivedFrom":[subQ1,subQ0]});Q53=makeQuery(id+"F6.imprint","IMPRINT",FACE,{"disambiguationData":[TD([[makeQuery(id+"F6.imprint","IMPRINT",EDGE,{"disambiguationData":[TD([[subQ2,-1.0]])],"derivedFrom":subQ1}),-1.0]])]});}
            var Q54;
            {var subQ0=sQuery(id+"F6.wireOp",EDGE,"E63.MirrorC");var subQ1=sQuery(id+"F6.wireOp",EDGE,"E30");var subQ2=makeQuery(id+"F6.imprint","INTERSECT",VERTEX,{"disambiguationData":[OD(0.0)],"derivedFrom":[subQ1,subQ0]});Q54=makeQuery(id+"F6.imprint","IMPRINT",FACE,{"disambiguationData":[TD([[makeQuery(id+"F6.imprint","IMPRINT",EDGE,{"disambiguationData":[TD([[subQ2,-1.0]])],"derivedFrom":subQ1}),-1.0]])]});}
            var Q55;
            {var subQ0=sQuery(id+"F6.wireOp",EDGE,"E63.MirrorC");var subQ1=sQuery(id+"F6.wireOp",EDGE,"E30");var subQ2=makeQuery(id+"F6.imprint","INTERSECT",VERTEX,{"disambiguationData":[OD(0.0)],"derivedFrom":[subQ1,subQ0]});Q55=makeQuery(id+"F6.imprint","IMPRINT",FACE,{"disambiguationData":[TD([[makeQuery(id+"F6.imprint","IMPRINT",EDGE,{"disambiguationData":[TD([[subQ2,-1.0]])],"derivedFrom":subQ1}),1.0]])]});}
            var Q56;
            {var subQ0=sQuery(id+"F6.wireOp",EDGE,"8a1fcb44-e85e-498d-8f55-af6f9230efa50.MirrorC");var subQ1=sQuery(id+"F6.wireOp",EDGE,"O4PxhCDK-rAjw-q9Xn-edEA-3iuNw1oMgCf9");var subQ2=makeQuery(id+"F6.imprint","INTERSECT",VERTEX,{"disambiguationData":[OD(0.0)],"derivedFrom":[subQ1,subQ0]});Q56=makeQuery(id+"F6.imprint","IMPRINT",FACE,{"disambiguationData":[TD([[makeQuery(id+"F6.imprint","IMPRINT",EDGE,{"disambiguationData":[TD([[subQ2,-1.0]])],"derivedFrom":subQ1}),-1.0]])]});}
            var Q57;
            {var subQ0=sQuery(id+"F6.wireOp",EDGE,"8a1fcb44-e85e-498d-8f55-af6f9230efa50.MirrorC");var subQ1=sQuery(id+"F6.wireOp",EDGE,"O4PxhCDK-rAjw-q9Xn-edEA-3iuNw1oMgCf9");var subQ2=makeQuery(id+"F6.imprint","INTERSECT",VERTEX,{"disambiguationData":[OD(0.0)],"derivedFrom":[subQ1,subQ0]});Q57=makeQuery(id+"F6.imprint","IMPRINT",FACE,{"disambiguationData":[TD([[makeQuery(id+"F6.imprint","IMPRINT",EDGE,{"disambiguationData":[TD([[subQ2,-1.0]])],"derivedFrom":subQ1}),1.0]])]});}
            var Q58;
            {var subQ0=sQuery(id+"F6.wireOp",EDGE,"769a7015-770e-43fc-8cfb-d75ca9284ac30.MirrorC");var subQ1=sQuery(id+"F6.wireOp",EDGE,"eJEehShp-Jti8-Zoit-Wwds-1zDcvAIGxxXx");var subQ2=makeQuery(id+"F6.imprint","INTERSECT",VERTEX,{"disambiguationData":[OD(0.0)],"derivedFrom":[subQ1,subQ0]});Q58=makeQuery(id+"F6.imprint","IMPRINT",FACE,{"disambiguationData":[TD([[makeQuery(id+"F6.imprint","IMPRINT",EDGE,{"disambiguationData":[TD([[subQ2,-1.0]])],"derivedFrom":subQ1}),-1.0]])]});}
            var Q59;
            {var subQ0=sQuery(id+"F6.wireOp",EDGE,"769a7015-770e-43fc-8cfb-d75ca9284ac30.MirrorC");var subQ1=sQuery(id+"F6.wireOp",EDGE,"eJEehShp-Jti8-Zoit-Wwds-1zDcvAIGxxXx");var subQ2=makeQuery(id+"F6.imprint","INTERSECT",VERTEX,{"disambiguationData":[OD(0.0)],"derivedFrom":[subQ1,subQ0]});Q59=makeQuery(id+"F6.imprint","IMPRINT",FACE,{"disambiguationData":[TD([[makeQuery(id+"F6.imprint","IMPRINT",EDGE,{"disambiguationData":[TD([[subQ2,-1.0]])],"derivedFrom":subQ1}),1.0]])]});}
            var Q60;
            {var subQ0=sQuery(id+"F6.wireOp",EDGE,"0039f2b9-d802-406d-b581-60a1267611bf0.MirrorC");var subQ1=sQuery(id+"F6.wireOp",EDGE,"eJEehShp-Jti8-Zoit-Wwds-1zDcvAIGxxXx");var subQ2=makeQuery(id+"F6.imprint","INTERSECT",VERTEX,{"disambiguationData":[OD(0.0)],"derivedFrom":[subQ1,subQ0]});Q60=makeQuery(id+"F6.imprint","IMPRINT",FACE,{"disambiguationData":[TD([[makeQuery(id+"F6.imprint","IMPRINT",EDGE,{"disambiguationData":[TD([[subQ2,-1.0]])],"derivedFrom":subQ1}),1.0]])]});}
            var Q61;
            {var subQ0=sQuery(id+"F6.wireOp",EDGE,"0039f2b9-d802-406d-b581-60a1267611bf0.MirrorC");var subQ1=sQuery(id+"F6.wireOp",EDGE,"eJEehShp-Jti8-Zoit-Wwds-1zDcvAIGxxXx");var subQ2=makeQuery(id+"F6.imprint","INTERSECT",VERTEX,{"disambiguationData":[OD(0.0)],"derivedFrom":[subQ1,subQ0]});Q61=makeQuery(id+"F6.imprint","IMPRINT",FACE,{"disambiguationData":[TD([[makeQuery(id+"F6.imprint","IMPRINT",EDGE,{"disambiguationData":[TD([[subQ2,-1.0]])],"derivedFrom":subQ1}),-1.0]])]});}
            var Q62;
            {var subQ0=sQuery(id+"F6.wireOp",EDGE,"0bd00658-e5c2-4675-bbe9-bbf1b690eca00.MirrorC");var subQ1=sQuery(id+"F6.wireOp",EDGE,"O4PxhCDK-rAjw-q9Xn-edEA-3iuNw1oMgCf9");var subQ2=makeQuery(id+"F6.imprint","INTERSECT",VERTEX,{"disambiguationData":[OD(0.0)],"derivedFrom":[subQ1,subQ0]});Q62=makeQuery(id+"F6.imprint","IMPRINT",FACE,{"disambiguationData":[TD([[makeQuery(id+"F6.imprint","IMPRINT",EDGE,{"disambiguationData":[TD([[subQ2,-1.0]])],"derivedFrom":subQ1}),1.0]])]});}
            var Q63;
            {var subQ0=sQuery(id+"F6.wireOp",EDGE,"0bd00658-e5c2-4675-bbe9-bbf1b690eca00.MirrorC");var subQ1=sQuery(id+"F6.wireOp",EDGE,"O4PxhCDK-rAjw-q9Xn-edEA-3iuNw1oMgCf9");var subQ2=makeQuery(id+"F6.imprint","INTERSECT",VERTEX,{"disambiguationData":[OD(0.0)],"derivedFrom":[subQ1,subQ0]});Q63=makeQuery(id+"F6.imprint","IMPRINT",FACE,{"disambiguationData":[TD([[makeQuery(id+"F6.imprint","IMPRINT",EDGE,{"disambiguationData":[TD([[subQ2,-1.0]])],"derivedFrom":subQ1}),-1.0]])]});}
            var Q64;
            {var subQ0=sQuery(id+"F6.wireOp",EDGE,"E64.MirrorC");var subQ1=sQuery(id+"F6.wireOp",EDGE,"E30");var subQ2=makeQuery(id+"F6.imprint","INTERSECT",VERTEX,{"disambiguationData":[OD(0.0)],"derivedFrom":[subQ1,subQ0]});Q64=makeQuery(id+"F6.imprint","IMPRINT",FACE,{"disambiguationData":[TD([[makeQuery(id+"F6.imprint","IMPRINT",EDGE,{"disambiguationData":[TD([[subQ2,-1.0]])],"derivedFrom":subQ1}),1.0]])]});}
            var Q65;
            {var subQ0=sQuery(id+"F6.wireOp",EDGE,"E64.MirrorC");var subQ1=sQuery(id+"F6.wireOp",EDGE,"E30");var subQ2=makeQuery(id+"F6.imprint","INTERSECT",VERTEX,{"disambiguationData":[OD(0.0)],"derivedFrom":[subQ1,subQ0]});Q65=makeQuery(id+"F6.imprint","IMPRINT",FACE,{"disambiguationData":[TD([[makeQuery(id+"F6.imprint","IMPRINT",EDGE,{"disambiguationData":[TD([[subQ2,-1.0]])],"derivedFrom":subQ1}),-1.0]])]});}
            var Q66;
            {var subQ0=sQuery(id+"F6.wireOp",EDGE,"E54.MirrorC");var subQ1=sQuery(id+"F6.wireOp",EDGE,"E29");var subQ2=makeQuery(id+"F6.imprint","INTERSECT",VERTEX,{"disambiguationData":[OD(0.0)],"derivedFrom":[subQ1,subQ0]});Q66=makeQuery(id+"F6.imprint","IMPRINT",FACE,{"disambiguationData":[TD([[makeQuery(id+"F6.imprint","IMPRINT",EDGE,{"disambiguationData":[TD([[subQ2,-1.0]])],"derivedFrom":subQ1}),-1.0]])]});}
            var Q67;
            {var subQ0=sQuery(id+"F6.wireOp",EDGE,"E54.MirrorC");var subQ1=sQuery(id+"F6.wireOp",EDGE,"E29");var subQ2=makeQuery(id+"F6.imprint","INTERSECT",VERTEX,{"disambiguationData":[OD(0.0)],"derivedFrom":[subQ1,subQ0]});Q67=makeQuery(id+"F6.imprint","IMPRINT",FACE,{"disambiguationData":[TD([[makeQuery(id+"F6.imprint","IMPRINT",EDGE,{"disambiguationData":[TD([[subQ2,-1.0]])],"derivedFrom":subQ1}),1.0]])]});}
            var Q68;
            {var subQ0=sQuery(id+"F6.wireOp",EDGE,"E59.MirrorC");var subQ1=sQuery(id+"F6.wireOp",EDGE,"E28");var subQ2=makeQuery(id+"F6.imprint","INTERSECT",VERTEX,{"disambiguationData":[OD(0.0)],"derivedFrom":[subQ1,subQ0]});Q68=makeQuery(id+"F6.imprint","IMPRINT",FACE,{"disambiguationData":[TD([[makeQuery(id+"F6.imprint","IMPRINT",EDGE,{"disambiguationData":[TD([[subQ2,-1.0]])],"derivedFrom":subQ1}),1.0]])]});}
            var Q69;
            {var subQ0=sQuery(id+"F6.wireOp",EDGE,"E59.MirrorC");var subQ1=sQuery(id+"F6.wireOp",EDGE,"E28");var subQ2=makeQuery(id+"F6.imprint","INTERSECT",VERTEX,{"disambiguationData":[OD(0.0)],"derivedFrom":[subQ1,subQ0]});Q69=makeQuery(id+"F6.imprint","IMPRINT",FACE,{"disambiguationData":[TD([[makeQuery(id+"F6.imprint","IMPRINT",EDGE,{"disambiguationData":[TD([[subQ2,-1.0]])],"derivedFrom":subQ1}),-1.0]])]});}
            var Q70;
            {var subQ0=sQuery(id+"F6.wireOp",EDGE,"E50.MirrorC");var subQ1=sQuery(id+"F6.wireOp",EDGE,"E27");var subQ2=makeQuery(id+"F6.imprint","INTERSECT",VERTEX,{"disambiguationData":[OD(0.0)],"derivedFrom":[subQ1,subQ0]});Q70=makeQuery(id+"F6.imprint","IMPRINT",FACE,{"disambiguationData":[TD([[makeQuery(id+"F6.imprint","IMPRINT",EDGE,{"disambiguationData":[TD([[subQ2,-1.0]])],"derivedFrom":subQ1}),-1.0]])]});}
            var Q71;
            {var subQ0=sQuery(id+"F6.wireOp",EDGE,"E50.MirrorC");var subQ1=sQuery(id+"F6.wireOp",EDGE,"E27");var subQ2=makeQuery(id+"F6.imprint","INTERSECT",VERTEX,{"disambiguationData":[OD(0.0)],"derivedFrom":[subQ1,subQ0]});Q71=makeQuery(id+"F6.imprint","IMPRINT",FACE,{"disambiguationData":[TD([[makeQuery(id+"F6.imprint","IMPRINT",EDGE,{"disambiguationData":[TD([[subQ2,-1.0]])],"derivedFrom":subQ1}),1.0]])]});}
            var Q72;
            {var subQ0=sQuery(id+"F6.wireOp",EDGE,"E44.MirrorC");var subQ1=sQuery(id+"F6.wireOp",EDGE,"E26");var subQ2=makeQuery(id+"F6.imprint","INTERSECT",VERTEX,{"disambiguationData":[OD(0.0)],"derivedFrom":[subQ1,subQ0]});Q72=makeQuery(id+"F6.imprint","IMPRINT",FACE,{"disambiguationData":[TD([[makeQuery(id+"F6.imprint","IMPRINT",EDGE,{"disambiguationData":[TD([[subQ2,-1.0]])],"derivedFrom":subQ1}),1.0]])]});}
            var Q73;
            {var subQ0=sQuery(id+"F6.wireOp",EDGE,"E44.MirrorC");var subQ1=sQuery(id+"F6.wireOp",EDGE,"E26");var subQ2=makeQuery(id+"F6.imprint","INTERSECT",VERTEX,{"disambiguationData":[OD(0.0)],"derivedFrom":[subQ1,subQ0]});Q73=makeQuery(id+"F6.imprint","IMPRINT",FACE,{"disambiguationData":[TD([[makeQuery(id+"F6.imprint","IMPRINT",EDGE,{"disambiguationData":[TD([[subQ2,-1.0]])],"derivedFrom":subQ1}),-1.0]])]});}
            var Q74;
            {var subQ0=sQuery(id+"F6.wireOp",EDGE,"E39.MirrorC");var subQ1=sQuery(id+"F6.wireOp",EDGE,"E25");var subQ2=makeQuery(id+"F6.imprint","INTERSECT",VERTEX,{"disambiguationData":[OD(0.0)],"derivedFrom":[subQ1,subQ0]});Q74=makeQuery(id+"F6.imprint","IMPRINT",FACE,{"disambiguationData":[TD([[makeQuery(id+"F6.imprint","IMPRINT",EDGE,{"disambiguationData":[TD([[subQ2,-1.0]])],"derivedFrom":subQ1}),1.0]])]});}
            var Q75;
            {var subQ0=sQuery(id+"F6.wireOp",EDGE,"E39.MirrorC");var subQ1=sQuery(id+"F6.wireOp",EDGE,"E25");var subQ2=makeQuery(id+"F6.imprint","INTERSECT",VERTEX,{"disambiguationData":[OD(0.0)],"derivedFrom":[subQ1,subQ0]});Q75=makeQuery(id+"F6.imprint","IMPRINT",FACE,{"disambiguationData":[TD([[makeQuery(id+"F6.imprint","IMPRINT",EDGE,{"disambiguationData":[TD([[subQ2,-1.0]])],"derivedFrom":subQ1}),-1.0]])]});}
            var Q76;
            {var subQ0=sQuery(id+"F6.wireOp",EDGE,"E34");var subQ1=sQuery(id+"F6.wireOp",EDGE,"E24");var subQ2=makeQuery(id+"F6.imprint","INTERSECT",VERTEX,{"disambiguationData":[OD(0.0)],"derivedFrom":[subQ1,subQ0]});Q76=makeQuery(id+"F6.imprint","IMPRINT",FACE,{"disambiguationData":[TD([[makeQuery(id+"F6.imprint","IMPRINT",EDGE,{"disambiguationData":[TD([[subQ2,-1.0]])],"derivedFrom":subQ1}),1.0]])]});}
            var Q77;
            {var subQ0=sQuery(id+"F6.wireOp",EDGE,"E34");var subQ1=sQuery(id+"F6.wireOp",EDGE,"E24");var subQ2=makeQuery(id+"F6.imprint","INTERSECT",VERTEX,{"disambiguationData":[OD(0.0)],"derivedFrom":[subQ1,subQ0]});Q77=makeQuery(id+"F6.imprint","IMPRINT",FACE,{"disambiguationData":[TD([[makeQuery(id+"F6.imprint","IMPRINT",EDGE,{"disambiguationData":[TD([[subQ2,-1.0]])],"derivedFrom":subQ1}),-1.0]])]});}
            var Q78;
            {var subQ0=sQuery(id+"F6.wireOp",EDGE,"E18");var subQ1=sQuery(id+"F6.wireOp",EDGE,"E17");var subQ2=makeQuery(id+"F6.imprint","INTERSECT",VERTEX,{"derivedFrom":[subQ1,subQ0]});Q78=makeQuery(id+"F6.imprint","IMPRINT",FACE,{"disambiguationData":[TD([[makeQuery(id+"F6.imprint","IMPRINT",EDGE,{"disambiguationData":[TD([[subQ2,1.0]])],"derivedFrom":subQ1}),1.0]])]});}
            var Q79;
            {var subQ0=sQuery(id+"F6.wireOp",EDGE,"E18");var subQ1=sQuery(id+"F6.wireOp",EDGE,"E17");var subQ2=makeQuery(id+"F6.imprint","INTERSECT",VERTEX,{"derivedFrom":[subQ1,subQ0]});Q79=makeQuery(id+"F6.imprint","IMPRINT",FACE,{"disambiguationData":[TD([[makeQuery(id+"F6.imprint","IMPRINT",EDGE,{"disambiguationData":[TD([[subQ2,1.0]])],"derivedFrom":subQ1}),-1.0]])]});}
            var Q80;
            Q80=makeQuery(id+"F6.imprint","IMPRINT",FACE,{"disambiguationData":[TD([[makeQuery(id+"F6.imprint","IMPRINT",EDGE,{"derivedFrom":sQuery(id+"F6.wireOp",EDGE,"E23")}),1.0]])]});
            var Q81;
            {var subQ0=sQuery(id+"F6.wireOp",EDGE,"E35");var subQ1=sQuery(id+"F6.wireOp",EDGE,"E24");var subQ2=makeQuery(id+"F6.imprint","INTERSECT",VERTEX,{"disambiguationData":[OD(0.0)],"derivedFrom":[subQ1,subQ0]});Q81=makeQuery(id+"F6.imprint","IMPRINT",FACE,{"disambiguationData":[TD([[makeQuery(id+"F6.imprint","IMPRINT",EDGE,{"disambiguationData":[TD([[subQ2,-1.0]])],"derivedFrom":subQ1}),-1.0]])]});}
            var Q82;
            {var subQ0=sQuery(id+"F6.wireOp",EDGE,"E35");var subQ1=sQuery(id+"F6.wireOp",EDGE,"E24");var subQ2=makeQuery(id+"F6.imprint","INTERSECT",VERTEX,{"disambiguationData":[OD(0.0)],"derivedFrom":[subQ1,subQ0]});Q82=makeQuery(id+"F6.imprint","IMPRINT",FACE,{"disambiguationData":[TD([[makeQuery(id+"F6.imprint","IMPRINT",EDGE,{"disambiguationData":[TD([[subQ2,-1.0]])],"derivedFrom":subQ1}),1.0]])]});}
            var Q83;
            {var subQ0=sQuery(id+"F6.wireOp",EDGE,"E40.MirrorC");var subQ1=sQuery(id+"F6.wireOp",EDGE,"E25");var subQ2=makeQuery(id+"F6.imprint","INTERSECT",VERTEX,{"disambiguationData":[OD(0.0)],"derivedFrom":[subQ1,subQ0]});Q83=makeQuery(id+"F6.imprint","IMPRINT",FACE,{"disambiguationData":[TD([[makeQuery(id+"F6.imprint","IMPRINT",EDGE,{"disambiguationData":[TD([[subQ2,-1.0]])],"derivedFrom":subQ1}),-1.0]])]});}
            var Q84;
            {var subQ0=sQuery(id+"F6.wireOp",EDGE,"E40.MirrorC");var subQ1=sQuery(id+"F6.wireOp",EDGE,"E25");var subQ2=makeQuery(id+"F6.imprint","INTERSECT",VERTEX,{"disambiguationData":[OD(0.0)],"derivedFrom":[subQ1,subQ0]});Q84=makeQuery(id+"F6.imprint","IMPRINT",FACE,{"disambiguationData":[TD([[makeQuery(id+"F6.imprint","IMPRINT",EDGE,{"disambiguationData":[TD([[subQ2,-1.0]])],"derivedFrom":subQ1}),1.0]])]});}
            var Q85;
            {var subQ0=sQuery(id+"F6.wireOp",EDGE,"E45.MirrorC");var subQ1=sQuery(id+"F6.wireOp",EDGE,"E26");var subQ2=makeQuery(id+"F6.imprint","INTERSECT",VERTEX,{"disambiguationData":[OD(0.0)],"derivedFrom":[subQ1,subQ0]});Q85=makeQuery(id+"F6.imprint","IMPRINT",FACE,{"disambiguationData":[TD([[makeQuery(id+"F6.imprint","IMPRINT",EDGE,{"disambiguationData":[TD([[subQ2,-1.0]])],"derivedFrom":subQ1}),-1.0]])]});}
            var Q86;
            {var subQ0=sQuery(id+"F6.wireOp",EDGE,"E45.MirrorC");var subQ1=sQuery(id+"F6.wireOp",EDGE,"E26");var subQ2=makeQuery(id+"F6.imprint","INTERSECT",VERTEX,{"disambiguationData":[OD(0.0)],"derivedFrom":[subQ1,subQ0]});Q86=makeQuery(id+"F6.imprint","IMPRINT",FACE,{"disambiguationData":[TD([[makeQuery(id+"F6.imprint","IMPRINT",EDGE,{"disambiguationData":[TD([[subQ2,-1.0]])],"derivedFrom":subQ1}),1.0]])]});}
            var Q87;
            {var subQ0=sQuery(id+"F6.wireOp",EDGE,"E49.MirrorC");var subQ1=sQuery(id+"F6.wireOp",EDGE,"E27");var subQ2=makeQuery(id+"F6.imprint","INTERSECT",VERTEX,{"disambiguationData":[OD(0.0)],"derivedFrom":[subQ1,subQ0]});Q87=makeQuery(id+"F6.imprint","IMPRINT",FACE,{"disambiguationData":[TD([[makeQuery(id+"F6.imprint","IMPRINT",EDGE,{"disambiguationData":[TD([[subQ2,-1.0]])],"derivedFrom":subQ1}),1.0]])]});}
            var Q88;
            {var subQ0=sQuery(id+"F6.wireOp",EDGE,"E49.MirrorC");var subQ1=sQuery(id+"F6.wireOp",EDGE,"E27");var subQ2=makeQuery(id+"F6.imprint","INTERSECT",VERTEX,{"disambiguationData":[OD(0.0)],"derivedFrom":[subQ1,subQ0]});Q88=makeQuery(id+"F6.imprint","IMPRINT",FACE,{"disambiguationData":[TD([[makeQuery(id+"F6.imprint","IMPRINT",EDGE,{"disambiguationData":[TD([[subQ2,-1.0]])],"derivedFrom":subQ1}),-1.0]])]});}
            var Q89;
            {var subQ0=sQuery(id+"F6.wireOp",EDGE,"E60.MirrorC");var subQ1=sQuery(id+"F6.wireOp",EDGE,"E28");var subQ2=makeQuery(id+"F6.imprint","INTERSECT",VERTEX,{"disambiguationData":[OD(0.0)],"derivedFrom":[subQ1,subQ0]});Q89=makeQuery(id+"F6.imprint","IMPRINT",FACE,{"disambiguationData":[TD([[makeQuery(id+"F6.imprint","IMPRINT",EDGE,{"disambiguationData":[TD([[subQ2,-1.0]])],"derivedFrom":subQ1}),-1.0]])]});}
            var Q90;
            {var subQ0=sQuery(id+"F6.wireOp",EDGE,"E60.MirrorC");var subQ1=sQuery(id+"F6.wireOp",EDGE,"E28");var subQ2=makeQuery(id+"F6.imprint","INTERSECT",VERTEX,{"disambiguationData":[OD(0.0)],"derivedFrom":[subQ1,subQ0]});Q90=makeQuery(id+"F6.imprint","IMPRINT",FACE,{"disambiguationData":[TD([[makeQuery(id+"F6.imprint","IMPRINT",EDGE,{"disambiguationData":[TD([[subQ2,-1.0]])],"derivedFrom":subQ1}),1.0]])]});}
            var Q91;
            {var subQ0=sQuery(id+"F6.wireOp",EDGE,"E55.MirrorC");var subQ1=sQuery(id+"F6.wireOp",EDGE,"E29");var subQ2=makeQuery(id+"F6.imprint","INTERSECT",VERTEX,{"disambiguationData":[OD(0.0)],"derivedFrom":[subQ1,subQ0]});Q91=makeQuery(id+"F6.imprint","IMPRINT",FACE,{"disambiguationData":[TD([[makeQuery(id+"F6.imprint","IMPRINT",EDGE,{"disambiguationData":[TD([[subQ2,-1.0]])],"derivedFrom":subQ1}),1.0]])]});}
            var Q92;
            {var subQ0=sQuery(id+"F6.wireOp",EDGE,"E55.MirrorC");var subQ1=sQuery(id+"F6.wireOp",EDGE,"E29");var subQ2=makeQuery(id+"F6.imprint","INTERSECT",VERTEX,{"disambiguationData":[OD(0.0)],"derivedFrom":[subQ1,subQ0]});Q92=makeQuery(id+"F6.imprint","IMPRINT",FACE,{"disambiguationData":[TD([[makeQuery(id+"F6.imprint","IMPRINT",EDGE,{"disambiguationData":[TD([[subQ2,-1.0]])],"derivedFrom":subQ1}),-1.0]])]});}
            var Q93;
            {var subQ0=sQuery(id+"F6.wireOp",EDGE,"E65.MirrorC");var subQ1=sQuery(id+"F6.wireOp",EDGE,"E30");var subQ2=makeQuery(id+"F6.imprint","INTERSECT",VERTEX,{"disambiguationData":[OD(0.0)],"derivedFrom":[subQ1,subQ0]});Q93=makeQuery(id+"F6.imprint","IMPRINT",FACE,{"disambiguationData":[TD([[makeQuery(id+"F6.imprint","IMPRINT",EDGE,{"disambiguationData":[TD([[subQ2,-1.0]])],"derivedFrom":subQ1}),-1.0]])]});}
            var Q94;
            {var subQ0=sQuery(id+"F6.wireOp",EDGE,"E65.MirrorC");var subQ1=sQuery(id+"F6.wireOp",EDGE,"E30");var subQ2=makeQuery(id+"F6.imprint","INTERSECT",VERTEX,{"disambiguationData":[OD(0.0)],"derivedFrom":[subQ1,subQ0]});Q94=makeQuery(id+"F6.imprint","IMPRINT",FACE,{"disambiguationData":[TD([[makeQuery(id+"F6.imprint","IMPRINT",EDGE,{"disambiguationData":[TD([[subQ2,-1.0]])],"derivedFrom":subQ1}),1.0]])]});}
            var Q95;
            {var subQ0=sQuery(id+"F6.wireOp",EDGE,"31c5dcd7-ded5-4874-9d90-4f231a2070e50.MirrorC");var subQ1=sQuery(id+"F6.wireOp",EDGE,"O4PxhCDK-rAjw-q9Xn-edEA-3iuNw1oMgCf9");var subQ2=makeQuery(id+"F6.imprint","INTERSECT",VERTEX,{"disambiguationData":[OD(0.0)],"derivedFrom":[subQ1,subQ0]});Q95=makeQuery(id+"F6.imprint","IMPRINT",FACE,{"disambiguationData":[TD([[makeQuery(id+"F6.imprint","IMPRINT",EDGE,{"disambiguationData":[TD([[subQ2,-1.0]])],"derivedFrom":subQ1}),-1.0]])]});}
            var Q96;
            {var subQ0=sQuery(id+"F6.wireOp",EDGE,"31c5dcd7-ded5-4874-9d90-4f231a2070e50.MirrorC");var subQ1=sQuery(id+"F6.wireOp",EDGE,"O4PxhCDK-rAjw-q9Xn-edEA-3iuNw1oMgCf9");var subQ2=makeQuery(id+"F6.imprint","INTERSECT",VERTEX,{"disambiguationData":[OD(0.0)],"derivedFrom":[subQ1,subQ0]});Q96=makeQuery(id+"F6.imprint","IMPRINT",FACE,{"disambiguationData":[TD([[makeQuery(id+"F6.imprint","IMPRINT",EDGE,{"disambiguationData":[TD([[subQ2,-1.0]])],"derivedFrom":subQ1}),1.0]])]});}
            var Q97;
            {var subQ0=sQuery(id+"F6.wireOp",EDGE,"24eafcb3-4e69-44cf-b0d4-83ff63781ba50.MirrorC");var subQ1=sQuery(id+"F6.wireOp",EDGE,"eJEehShp-Jti8-Zoit-Wwds-1zDcvAIGxxXx");var subQ2=makeQuery(id+"F6.imprint","INTERSECT",VERTEX,{"disambiguationData":[OD(0.0)],"derivedFrom":[subQ1,subQ0]});Q97=makeQuery(id+"F6.imprint","IMPRINT",FACE,{"disambiguationData":[TD([[makeQuery(id+"F6.imprint","IMPRINT",EDGE,{"disambiguationData":[TD([[subQ2,-1.0]])],"derivedFrom":subQ1}),-1.0]])]});}
            var Q98;
            {var subQ0=sQuery(id+"F6.wireOp",EDGE,"24eafcb3-4e69-44cf-b0d4-83ff63781ba50.MirrorC");var subQ1=sQuery(id+"F6.wireOp",EDGE,"eJEehShp-Jti8-Zoit-Wwds-1zDcvAIGxxXx");var subQ2=makeQuery(id+"F6.imprint","INTERSECT",VERTEX,{"disambiguationData":[OD(0.0)],"derivedFrom":[subQ1,subQ0]});Q98=makeQuery(id+"F6.imprint","IMPRINT",FACE,{"disambiguationData":[TD([[makeQuery(id+"F6.imprint","IMPRINT",EDGE,{"disambiguationData":[TD([[subQ2,-1.0]])],"derivedFrom":subQ1}),1.0]])]});}
            extrude(context, id + "F7", {"entities" : qUnion([Q0, Q1, Q2, Q3, Q4, Q5, Q6, Q7, Q8, Q9, Q10, Q11, Q12, Q13, Q14, Q15, Q16, Q17, Q18, Q19, Q20, Q21, Q22, Q23, Q24, Q25, Q26, Q27, Q28, Q29, Q30, Q31, Q32, Q33, Q34, Q35, Q36, Q37, Q38, Q39, Q40, Q41, Q42, Q43, Q44, Q45, Q46, Q47, Q48, Q49, Q50, Q51, Q52, Q53, Q54, Q55, Q56, Q57, Q58, Q59, Q60, Q61, Q62, Q63, Q64, Q65, Q66, Q67, Q68, Q69, Q70, Q71, Q72, Q73, Q74, Q75, Q76, Q77, Q78, Q79, Q80, Q81, Q82, Q83, Q84, Q85, Q86, Q87, Q88, Q89, Q90, Q91, Q92, Q93, Q94, Q95, Q96, Q97, Q98]), "operationType" : NewBodyOperationType.REMOVE, "oppositeDirection" : true, "depth" : 25 * mm, "offsetDistance" : 25 * mm});
        }
    });
